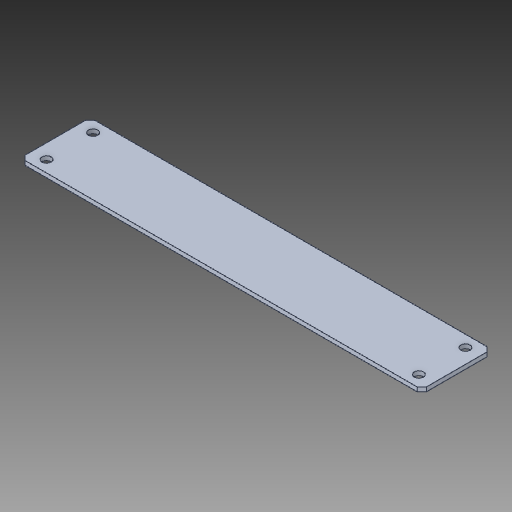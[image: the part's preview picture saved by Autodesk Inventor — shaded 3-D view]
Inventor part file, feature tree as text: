
AUTODESK INVENTOR PART (.ipt)
format: ipt  version: 2017.1 (Build 211199000, 199)  size: 87,040 bytes
history: native  units: in
note: dims shown in document units (in); Inventor stores cm internally (conversion verified against a paired STEP export)
features: chamfer x1
ambient origin geometry x8: Origin, YZ Plane, XZ Plane, XY Plane, X Axis, Y Axis, Z Axis, Center Point
bodies: Solid1 (feature_tree)
feature tree (1):
  chamfer  "Chamfer1"  [1 undecoded]
note: 1 required parameter value undecoded (feature->parameter linkage not recoverable at this tier; creation-order binding heuristic only, values carry confidence <= 0.55)
